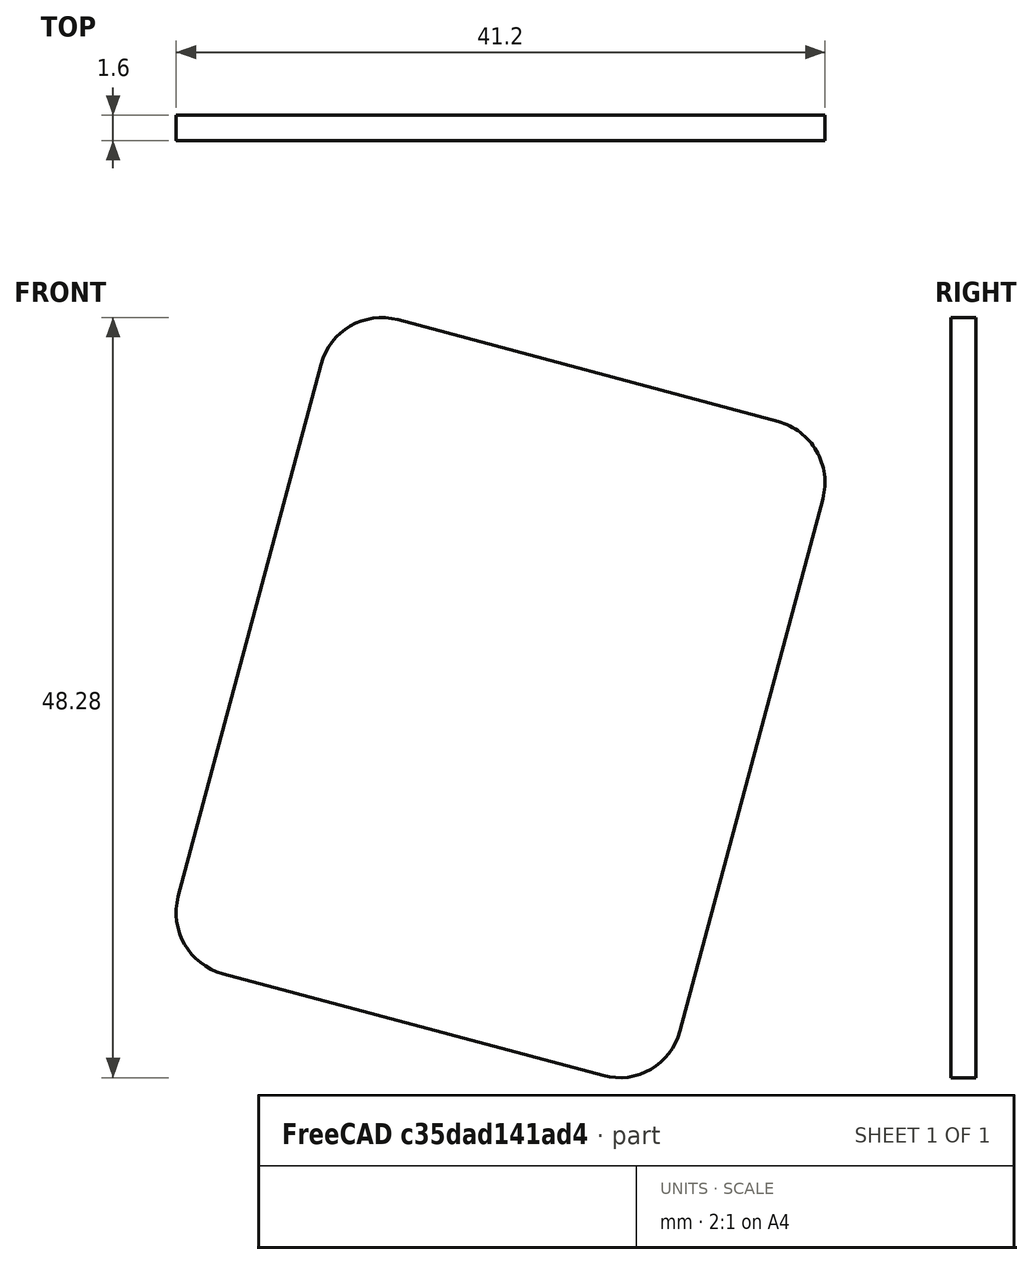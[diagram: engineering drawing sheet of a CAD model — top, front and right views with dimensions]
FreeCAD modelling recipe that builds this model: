
FCSTD DOCUMENT  (FreeCAD 0.20R29603 (Git))
Label: Right THrottle Switches and Hat Layout
Comment: Proposed layout of switches and hat for THQ Hotas Right Throttle Project
License: Creative Commons Attribution-NonCommercial 4.0 International License.
LicenseURL: http://creativecommons.org/licenses/by-nc/4.0/
objects: Mesh::Feature×6, Sketcher::SketchObject×1, PartDesign::Pad×1, PartDesign::Body×1
note: 4 computed .brp shape members not serialized (recipe doc carries the construction recipe); baked Part::Feature solids carry a one-line shape summary decoded from their .brp

FEATURE [Mesh::Feature] VKB_THQ_Hotas_v1___RH_Side_Panel  label="VKB THQ Hotas v1 - RH Side Panel"
FEATURE [Mesh::Feature] China_HAT  label="Speedbrake"
  Placement = pos=(14,-60,-61) rot=(0.57735,0.57735,-0.57735;2.0944rad)
FEATURE [Mesh::Feature] Comms_HAT
  Placement = pos=(-36,-57,42) rot=(0,0,1;3.14159rad)
FEATURE [Mesh::Feature] SB_HAT  label="Boat"
  Placement = pos=(19,-60,-45) rot=(0.57735,0.57735,-0.57735;2.0944rad)
FEATURE [Mesh::Feature] VKB_THQ_Hotas_v1___RH_Body  label="VKB THQ Hotas v1 - RH Body"
FEATURE [Sketcher::SketchObject] Sketch
  FullyConstrained = true
  MapMode = 5
  Placement = pos=(0,0,0) rot=(1,0,0;1.5708rad)
  Support = -> [XZ_Plane]
  sketch-geometry (8):
    g0: LineSegment StartX=-12.5 StartY=21.5 StartZ=0 EndX=12.5 EndY=21.5 EndZ=0
    g1: LineSegment StartX=16.5 StartY=17.5 StartZ=0 EndX=16.5 EndY=-17.5 EndZ=0
    g2: LineSegment StartX=12.5 StartY=-21.5 StartZ=0 EndX=-12.5 EndY=-21.5 EndZ=0
    g3: LineSegment StartX=-16.5 StartY=-17.5 StartZ=0 EndX=-16.5 EndY=17.5 EndZ=0
    g4: ArcOfCircle CenterX=-12.5 CenterY=17.5 CenterZ=0 NormalX=0 NormalY=0 NormalZ=1 AngleXU=0 Radius=4 StartAngle=1.5708 EndAngle=3.14159
    g5: ArcOfCircle CenterX=12.5 CenterY=17.5 CenterZ=0 NormalX=0 NormalY=0 NormalZ=1 AngleXU=0 Radius=4 StartAngle=-9e-16 EndAngle=1.5708
    g6: ArcOfCircle CenterX=-12.5 CenterY=-17.5 CenterZ=0 NormalX=0 NormalY=0 NormalZ=1 AngleXU=0 Radius=4 StartAngle=3.14159 EndAngle=4.71239
    g7: ArcOfCircle CenterX=12.5 CenterY=-17.5 CenterZ=0 NormalX=0 NormalY=0 NormalZ=1 AngleXU=0 Radius=4 StartAngle=4.71239 EndAngle=6.28319
  constraints (18):
    c: Horizontal(g0)
    c: Horizontal(g2)
    c: Vertical(g3)
    c: Tangent(g0,g4) = 1.5708
    c: Tangent(g3,g4) = 1.5708
    c: Radius(g4) = 4
    c: Tangent(g0,g5) = 1.5708
    c: Tangent(g1,g5) = 1.5708
    c: Tangent(g2,g6) = 1.5708
    c: Tangent(g3,g6) = 1.5708
    c: Radius(g6) = 4
    c: Tangent(g1,g7) = 1.5708
    c: Tangent(g2,g7) = 1.5708
    c: Radius(g7) = 4
    c: Symmetric(g3,g1,g-2)
    c: DistanceX(g0,g0) = 25
    c: DistanceY(g1,g1) = 35
    c: Symmetric(g1,g1,g-1)
FEATURE [PartDesign::Pad] Pad001  label="Rev 1.4"
  Direction = (0,-1,2e-16)
  Length = 1.6
  Length2 = 10
  Placement = pos=(0,0,0) rot=(1,0,0;1.5708rad)
  Profile = -> Sketch
  ReferenceAxis = -> Sketch [N_Axis]
  Type = 0
FEATURE [PartDesign::Body] Body  label="Main Board"
  Group = -> [Sketch,Pad001]
  Origin = -> Origin
  Placement = pos=(-8.93974,-2,26.7562) rot=(0,1,0;0.261799rad)
  Tip = -> Pad001
FEATURE [Mesh::Feature] Stadium_HAT
  Placement = pos=(44,-57,51) rot=(1,0,0;3.14159rad)
